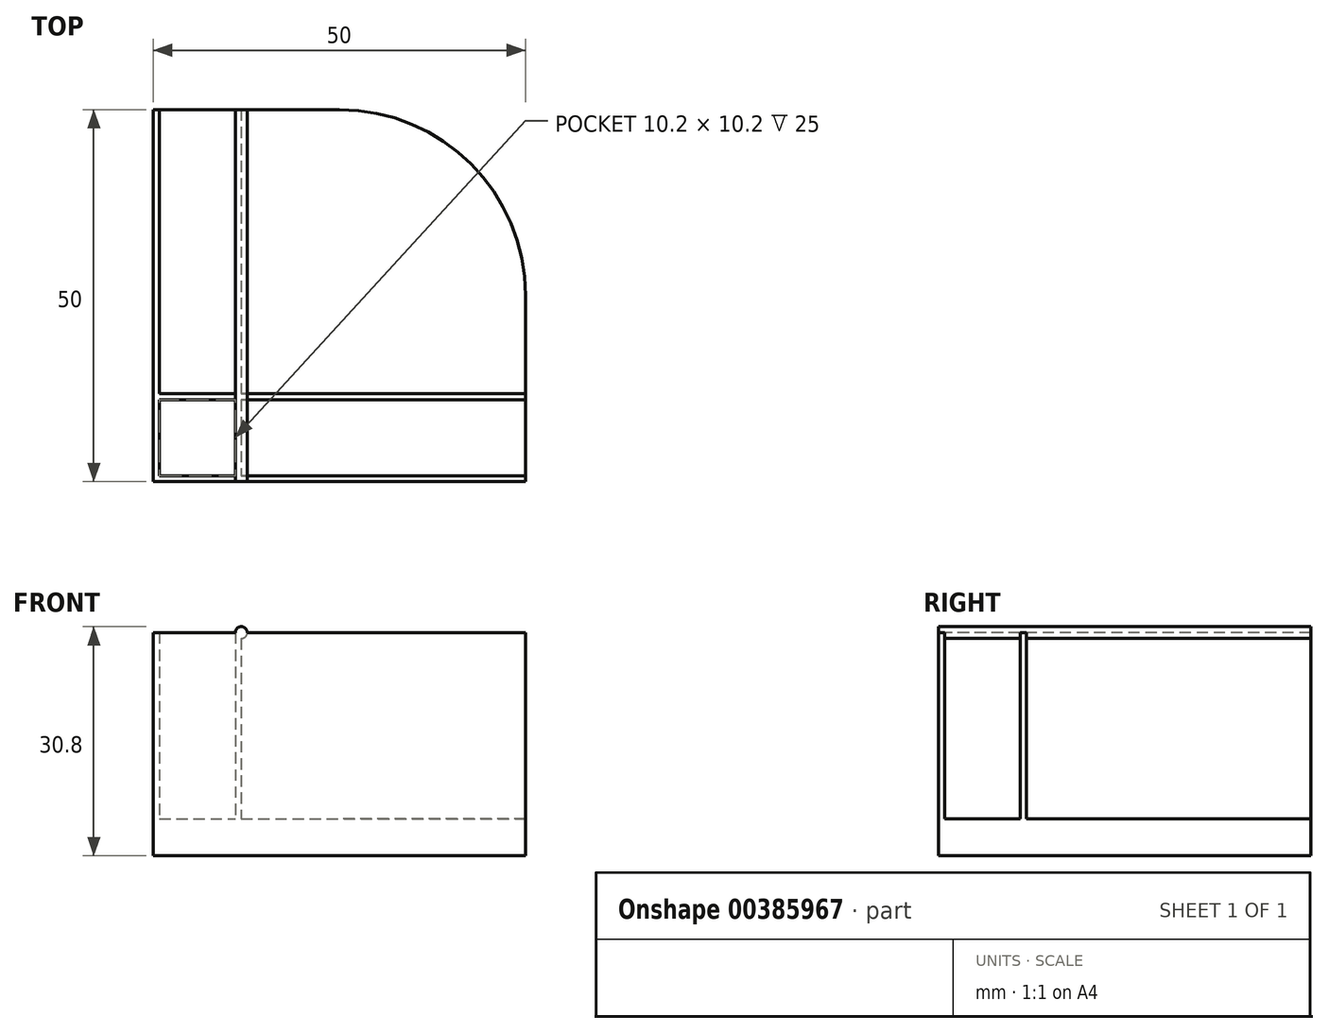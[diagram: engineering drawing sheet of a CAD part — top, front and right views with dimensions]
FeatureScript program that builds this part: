
annotation { "Feature Type Name" : "Feature", "Feature Type Description" : "" }
export const myFeature = defineFeature(function(context is Context, id is Id, definition is map)
    precondition{}
    {
        {
            var Q0;
            Q0=qCreatedBy(makeId("Top.planeOp"),FACE);
            var sketch = newSketch(context, id + "F0", { "sketchPlane" : qUnion([Q0])});
            skLineSegment(sketch, "E0.bottom", {"start": v(-25, 25) * mm, "end": v(0, 25) * mm});
            skLineSegment(sketch, "E0.top", {"start": v(-25, -25) * mm, "end": v(25, -25) * mm});
            skLineSegment(sketch, "E0.left", {"start": v(-25, 25) * mm, "end": v(-25, -25) * mm});
            skLineSegment(sketch, "E0.right", {"start": v(25, 0) * mm, "end": v(25, -25) * mm});
            skPoint(sketch, "E0.middle", {"position": v(0, 0) * mm});
            skPoint(sketch, "E1.visualSharp", {"position": v(25, 25) * mm});
            skArc(sketch, "E1.filletArc", {"start": v(25, 0) * mm, "mid": v(17.68, 17.68) * mm, "end": v(0, 25) * mm});
            skSolve(sketch);
        }
        {
            var Q0;
            Q0=makeQuery(id+"F0.imprint","IMPRINT",FACE,{"disambiguationData":[TD([[makeQuery(id+"F0.imprint","IMPRINT",EDGE,{"derivedFrom":sQuery(id+"F0.wireOp",EDGE,"E0.bottom")}),-1.0]])]});
            extrude(context, id + "F1", {"entities" : qUnion([Q0]), "depth" : 5 * mm});
        }
        {
            var Q0;
            Q0=makeQuery(id+"F1.opExtrude","CAP_FACE",FACE,{"disambiguationData":[OSD([sQuery(id+"F0.wireOp",EDGE,"E0.bottom"),sQuery(id+"F0.wireOp",EDGE,"E0.top"),sQuery(id+"F0.wireOp",EDGE,"E0.left"),sQuery(id+"F0.wireOp",EDGE,"E0.right"),sQuery(id+"F0.wireOp",EDGE,"E1.filletArc")])],"isStart":false});
            var sketch = newSketch(context, id + "F2", { "sketchPlane" : qUnion([Q0])});
            skLineSegment(sketch, "E2.left", {"start": v(-24.2, 25) * mm, "end": v(-24.2, -13.2) * mm});
            skLineSegment(sketch, "E2.right", {"start": v(-14, 25) * mm, "end": v(-14, -13.2) * mm});
            skLineSegment(sketch, "E3.bottom", {"start": v(-24.2, -14) * mm, "end": v(-14, -14) * mm});
            skLineSegment(sketch, "E4", {"start": v(-24.2, -13.2) * mm, "end": v(-14, -13.2) * mm});
            skLineSegment(sketch, "E5", {"start": v(-13.2, 25) * mm, "end": v(-13.2, -13.2) * mm});
            skLineSegment(sketch, "E6.trimOffspring", {"start": v(-13.2, -24.2) * mm, "end": v(25, -24.2) * mm});
            skLineSegment(sketch, "E7.trimOffspring", {"start": v(-14, -14) * mm, "end": v(-14, -24.2) * mm});
            skLineSegment(sketch, "E8.trimOffspring", {"start": v(-13.2, -14) * mm, "end": v(-13.2, -24.2) * mm});
            skLineSegment(sketch, "E9.trimOffspring", {"start": v(-13.2, -13.2) * mm, "end": v(25, -13.2) * mm});
            skLineSegment(sketch, "E10.trimOffspring", {"start": v(-13.2, -14) * mm, "end": v(25, -14) * mm});
            skLineSegment(sketch, "E11", {"start": v(-14, -24.2) * mm, "end": v(-24.2, -24.2) * mm});
            skLineSegment(sketch, "E12", {"start": v(-24.2, -14) * mm, "end": v(-24.2, -24.2) * mm});
            skSolve(sketch);
        }
        {
            var Q0;
            {var subQ4=sQuery(id+"F2.wireOp",EDGE,"E2.left");Q0=makeQuery(id+"F2.imprint","IMPRINT",FACE,{"disambiguationData":[TD([[makeQuery(id+"F2.imprint","IMPRINT",EDGE,{"derivedFrom":subQ4}),-1.0]])]});}
            extrude(context, id + "F3", {"entities" : qUnion([Q0]), "operationType" : NewBodyOperationType.ADD, "depth" : 25 * mm});
        }
        {
            var Q0;
            {var subQ0=sQuery(id+"F0.wireOp",EDGE,"E0.bottom");var subQ1=makeQuery(id+"F1.opExtrude","CAP_EDGE",EDGE,{"disambiguationData":[OSD([subQ0])],"isStart":false});Q0=makeQuery(id+"F3.boolean.opBoolean","MERGE",FACE,{"derivedFrom":[makeQuery(id+"F1.opExtrude","SWEPT_FACE",FACE,{"disambiguationData":[OSD([subQ0])]}),makeQuery(id+"F3.opExtrude","SWEPT_FACE",FACE,{"disambiguationData":[OSD([subQ0]),TDD([makeQuery(id+"F2.imprint","IMPRINT",EDGE,{"disambiguationData":[TD([[makeQuery(id+"F2.imprint","INTERSECT",VERTEX,{"derivedFrom":[subQ1,makeQuery(id+"F1.opExtrude","CAP_EDGE",EDGE,{"disambiguationData":[OSD([sQuery(id+"F0.wireOp",EDGE,"E0.left")])],"isStart":false})]}),-1.0]])],"derivedFrom":subQ1})])]}),makeQuery(id+"F3.opExtrude","SWEPT_FACE",FACE,{"disambiguationData":[OSD([subQ0]),TDD([makeQuery(id+"F2.imprint","IMPRINT",EDGE,{"disambiguationData":[TD([[makeQuery(id+"F2.imprint","INTERSECT",VERTEX,{"derivedFrom":[subQ1,sQuery(id+"F2.wireOp",EDGE,"E2.right")]}),-1.0]])],"derivedFrom":subQ1})])]})]});}
            var sketch = newSketch(context, id + "F4", { "sketchPlane" : qUnion([Q0])});
            skCircle(sketch, "E13", {"center": v(13.2, 30) * mm, "radius": 0.8 * mm});
            skSolve(sketch);
        }
        {
            var Q0;
            {var subQ1=sQuery(id+"F2.wireOp",EDGE,"E2.right");var subQ2=sQuery(id+"F0.wireOp",EDGE,"E0.bottom");var subQ3=makeQuery(id+"F1.opExtrude","CAP_EDGE",EDGE,{"disambiguationData":[OSD([subQ2])],"isStart":false});var subQ5=makeQuery(id+"F3.opExtrude","CAP_EDGE",EDGE,{"disambiguationData":[OSD([subQ2]),TDD([makeQuery(id+"F2.imprint","IMPRINT",EDGE,{"disambiguationData":[TD([[makeQuery(id+"F2.imprint","INTERSECT",VERTEX,{"derivedFrom":[subQ3,subQ1]}),-1.0]])],"derivedFrom":subQ3})])],"isStart":false});Q0=makeQuery(id+"F4.imprint","IMPRINT",FACE,{"disambiguationData":[TD([[makeQuery(id+"F4.imprint","IMPRINT",EDGE,{"derivedFrom":subQ5}),-1.0]])]});}
            extrude(context, id + "F5", {"entities" : qUnion([Q0]), "operationType" : NewBodyOperationType.ADD, "oppositeDirection" : true, "depth" : 50 * mm});
        }
    });
